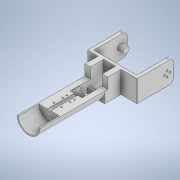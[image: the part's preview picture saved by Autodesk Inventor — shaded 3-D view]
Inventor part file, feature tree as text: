
AUTODESK INVENTOR PART (.ipt)
format: ipt  version: 2022 (Build 260153000, 153)  size: 391,168 bytes
history: native  units: mm
features: sketch x22, extrude x21, fillet x2, plane x1
ambient origin geometry x8: Origin, YZ Plane, XZ Plane, XY Plane, X Axis, Y Axis, Z Axis, Center Point
bodies: Solid1 (feature_tree)
feature tree (46):
  extrude  "Extrusion1"  Depth=80.0mm
  extrude  "Extrusion2"  Depth=40.0mm TaperAngle=0.0deg
  extrude  "Extrusion3"  Depth=3.0mm
  fillet  "Fillet1"  Radius=40.0mm
  extrude  "Extrusion4"  Depth=4.0mm
  extrude  "Extrusion5"  Depth=10.0mm TaperAngle=0.0deg
  extrude  "Extrusion6"  Depth=11.0mm
  extrude  "Extrusion7"  Depth=11.0mm
  extrude  "Extrusion8"  Depth=24.0mm TaperAngle=0.0deg
  extrude  "Extrusion9"  Depth=6.0mm TaperAngle=0.0deg
  extrude  "Extrusion10"  Depth=33.7mm
  extrude  "Extrusion11"  Depth=11.0mm TaperAngle=0.0deg
  extrude  "Extrusion12"  Depth=50.0mm TaperAngle=0.0deg
  fillet  "Fillet3"  Radius=50.0mm
  extrude  "Extrusion19"  Depth=38.0mm
  extrude  "Extrusion20"  Depth=6.2mm TaperAngle=0.0deg
  extrude  "Extrusion21"  Depth=10.0mm TaperAngle=0.0deg
  extrude  "Extrusion22"  Depth=10.0mm TaperAngle=0.0deg
  extrude  "Extrusion23"  Depth=10.0mm TaperAngle=0.0deg
  extrude  "Extrusion24"  Depth=4.0mm
  extrude  "Extrusion25"  Depth=6.0mm
  sketch  "Sketch27"  dims[d92=10.0mm d93=0.0mm d95=4.4mm]
  plane  "Work Plane2"
  extrude  "Extrusion26"  Depth=10.0mm
  extrude  "Extrusion27"  Depth=4.0mm TaperAngle=0.0deg
  sketch  "Sketch1"  dims[d0=62.0mm d1=80.0mm]
  sketch  "Sketch2"  dims[d2=6.0mm d3=40.0mm d4=0.0mm]
  sketch  "Sketch3"  dims[d5=62.0mm d9=3.0mm d10=40.0mm d12=360.0deg]
  sketch  "Sketch4"  dims[d14=40.0mm d15=0.0mm d16=4.0mm]
  sketch  "Sketch5"  dims[d18=11.5mm d19=10.0mm d20=0.0mm]
  sketch  "Sketch6"  dims[d21=8.0mm d22=11.0mm]
  sketch  "Sketch8"  dims[d23=11.0mm d24=5.0mm]
  sketch  "Sketch9"  dims[d25=5.0mm d26=24.0mm d27=0.0mm]
  sketch  "Sketch10"  dims[d29=6.0mm d30=6.0mm d31=0.0mm]
  sketch  "Sketch11"  dims[d32=13.8mm d33=0.0mm d37=33.7mm]
  sketch  "Sketch12"  dims[d38=11.0mm d39=13.8mm d40=0.0mm]
  sketch  "Sketch13"  dims[d41=6.0mm d42=50.0mm d43=0.0mm d44=50.0mm d45=0.0mm]
  sketch  "Sketch20"  dims[d47=36.0mm d48=0.0mm d49=38.0mm]
  sketch  "Sketch21"  dims[d50=32.0mm d51=0.0mm d52=6.2mm d53=0.0mm]
  sketch  "Sketch22"  dims[d63=1.0mm d69=10.0mm d70=0.0mm]
  sketch  "Sketch23"  dims[d71=10.0mm d72=0.0mm d73=10.0mm d74=0.0mm]
  sketch  "Sketch24"  dims[d75=10.0mm d76=0.0mm d77=10.0mm d78=0.0mm]
  sketch  "Sketch25"  dims[d84=0.0mm d85=0.0mm d86=4.0mm]
  sketch  "Sketch26"  dims[d90=2.5mm d91=6.0mm]
  sketch  "Sketch28"  dims[d96=4.2mm d97=0.0mm d98=4.0mm d99=0.0mm]
  sketch  "Sketch29"
